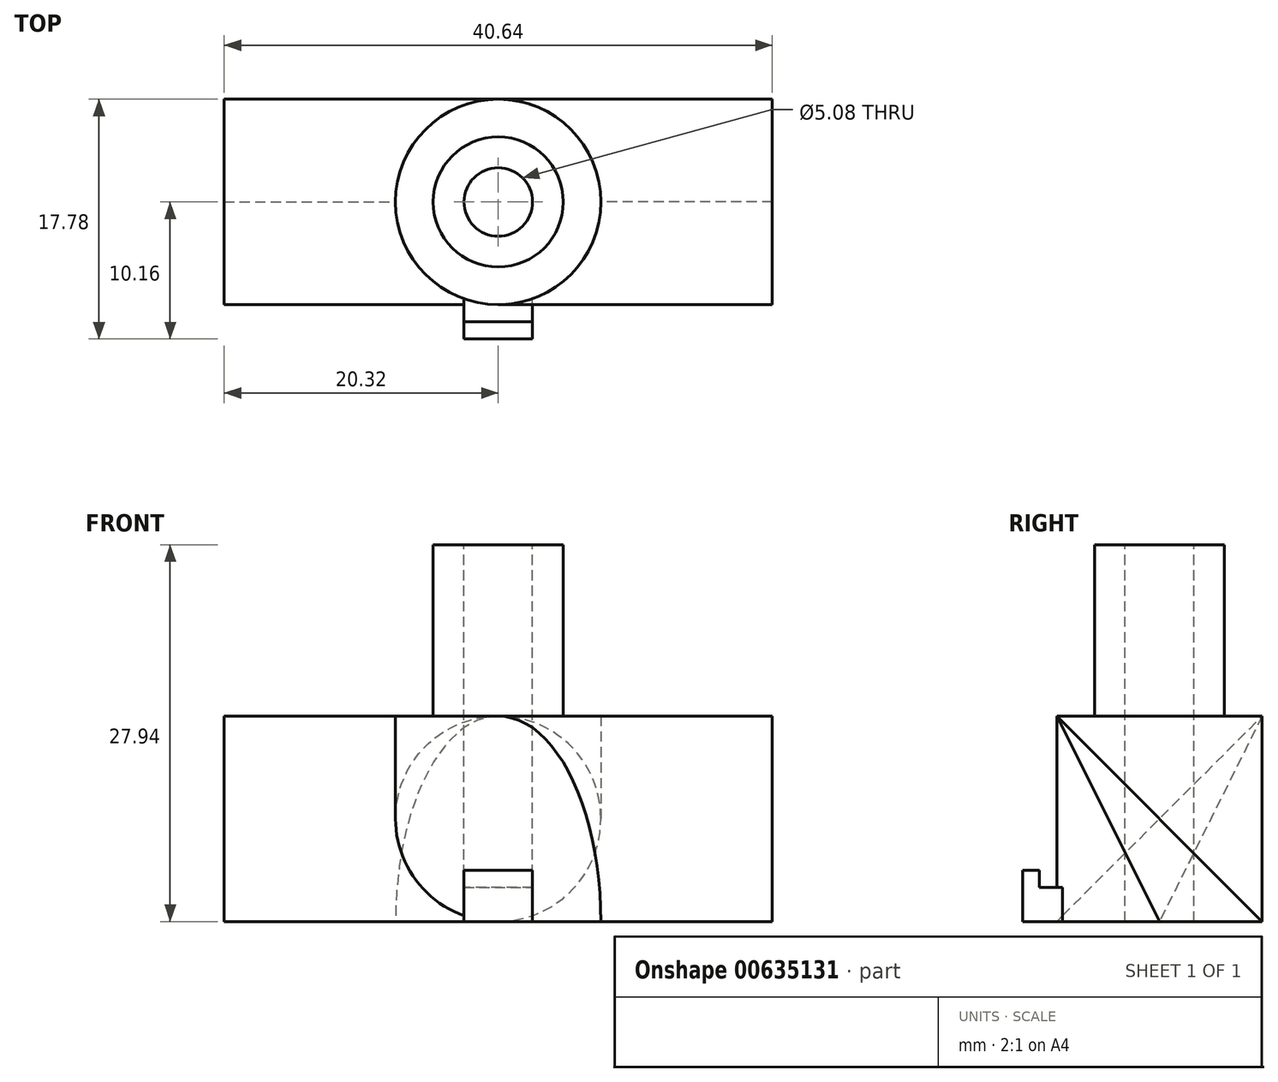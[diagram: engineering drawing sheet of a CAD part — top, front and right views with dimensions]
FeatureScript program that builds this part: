
annotation { "Feature Type Name" : "Feature", "Feature Type Description" : "" }
export const myFeature = defineFeature(function(context is Context, id is Id, definition is map)
    precondition{}
    {
        {
            var Q0;
            Q0=qCreatedBy(makeId("Top.planeOp"),FACE);
            var sketch = newSketch(context, id + "F0", { "sketchPlane" : qUnion([Q0])});
            skCircle(sketch, "E0", {"center": v(0, 0) * mm, "radius": 7.62 * mm});
            skSolve(sketch);
        }
        {
            var Q0;
            Q0=makeQuery(id+"F0.imprint","IMPRINT",FACE,{"disambiguationData":[TD([[makeQuery(id+"F0.imprint","IMPRINT",EDGE,{"derivedFrom":sQuery(id+"F0.wireOp",EDGE,"E0")}),1.0]])]});
            extrude(context, id + "F1", {"entities" : qUnion([Q0]), "depth" : 15.24 * mm, "offsetDistance" : 25.4 * mm});
        }
        {
            var Q0;
            Q0=qCreatedBy(makeId("Right.planeOp"),FACE);
            var sketch = newSketch(context, id + "F2", { "sketchPlane" : qUnion([Q0])});
            skLineSegment(sketch, "E1", {"start": v(0, 0) * mm, "end": v(7.62, 0) * mm});
            skLineSegment(sketch, "E2", {"start": v(7.62, 0) * mm, "end": v(-7.62, 15.24) * mm});
            skLineSegment(sketch, "E3", {"start": v(-7.62, 15.24) * mm, "end": v(0, 0) * mm});
            skSolve(sketch);
        }
        {
            var Q0;
            Q0=qSketchRegion(id+"F2",true);
            extrude(context, id + "F3", {"entities" : qUnion([Q0]), "depth" : 20.32 * mm, "offsetDistance" : 25.4 * mm});
        }
        {
            var Q0;
            Q0=qCreatedBy(makeId("Front.planeOp"),FACE);
            var sketch = newSketch(context, id + "F4", { "sketchPlane" : qUnion([Q0])});
            skLineSegment(sketch, "E4", {"start": v(0, 0) * mm, "end": v(0, 35.17) * mm, "construction": true});
            skSolve(sketch);
        }
        {
            var Q0;
            Q0=makeQuery(id+"F3.opExtrude","SWEPT_BODY",BODY,{"disambiguationData":[OSD([sQuery(id+"F2.wireOp",EDGE,"E1"),sQuery(id+"F2.wireOp",EDGE,"E2"),sQuery(id+"F2.wireOp",EDGE,"E3")])]});
            var Q1;
            Q1=sQuery(id+"F4.wireOp",EDGE,"E4");
            circularPattern(context, id + "F5", {"operationType" : NewBodyOperationType.ADD, "entities" : qUnion([Q0]), "axis" : qUnion([Q1]), "angle" : 360 * degree, "instanceCount" : 2, "equalSpace" : true});
        }
        {
            var Q0;
            Q0=qCreatedBy(makeId("Front.planeOp"),FACE);
            var sketch = newSketch(context, id + "F6", { "sketchPlane" : qUnion([Q0])});
            skLineSegment(sketch, "E5.bottom", {"start": v(-2.54, 2.54) * mm, "end": v(2.54, 2.54) * mm});
            skLineSegment(sketch, "E5.top", {"start": v(-2.54, 0) * mm, "end": v(2.54, 0) * mm});
            skLineSegment(sketch, "E5.left", {"start": v(-2.54, 2.54) * mm, "end": v(-2.54, 0) * mm});
            skLineSegment(sketch, "E5.right", {"start": v(2.54, 2.54) * mm, "end": v(2.54, 0) * mm});
            skSolve(sketch);
        }
        {
            var Q0;
            Q0=qSketchRegion(id+"F6",true);
            extrude(context, id + "F7", {"entities" : qUnion([Q0]), "operationType" : NewBodyOperationType.ADD, "depth" : 10.16 * mm, "offsetDistance" : 25.4 * mm});
        }
        {
            var Q0;
            Q0=makeQuery(id+"F7.opExtrude","SWEPT_FACE",FACE,{"disambiguationData":[OSD([sQuery(id+"F6.wireOp",EDGE,"E5.bottom")])]});
            var sketch = newSketch(context, id + "F8", { "sketchPlane" : qUnion([Q0])});
            skLineSegment(sketch, "E6.bottom", {"start": v(2.54, -10.16) * mm, "end": v(-2.54, -10.16) * mm});
            skLineSegment(sketch, "E6.top", {"start": v(2.54, -8.9) * mm, "end": v(-2.54, -8.9) * mm});
            skLineSegment(sketch, "E6.left", {"start": v(2.54, -10.16) * mm, "end": v(2.54, -8.9) * mm});
            skLineSegment(sketch, "E6.right", {"start": v(-2.54, -10.16) * mm, "end": v(-2.54, -8.9) * mm});
            skSolve(sketch);
        }
        {
            var Q0;
            Q0=makeQuery(id+"F8.imprint","IMPRINT",FACE,{"disambiguationData":[TD([[makeQuery(id+"F8.imprint","IMPRINT",EDGE,{"derivedFrom":sQuery(id+"F8.wireOp",EDGE,"E6.bottom")}),1.0]])]});
            extrude(context, id + "F9", {"entities" : qUnion([Q0]), "operationType" : NewBodyOperationType.ADD, "depth" : 1.27 * mm, "offsetDistance" : 25.4 * mm});
        }
        {
            var Q0;
            Q0=makeQuery(id+"F1.opExtrude","CAP_FACE",FACE,{"disambiguationData":[OSD([sQuery(id+"F0.wireOp",EDGE,"E0")])],"isStart":false});
            var sketch = newSketch(context, id + "F10", { "sketchPlane" : qUnion([Q0])});
            skCircle(sketch, "E7", {"center": v(0, 0) * mm, "radius": 2.54 * mm});
            skSolve(sketch);
        }
        {
            var Q0;
            Q0=qSketchRegion(id+"F10",true);
            extrude(context, id + "F11", {"entities" : qUnion([Q0]), "operationType" : NewBodyOperationType.REMOVE, "endBound" : BoundingType.THROUGH_ALL, "oppositeDirection" : true, "depth" : 13.97 * mm, "offsetDistance" : 25.4 * mm});
        }
        {
            var Q0;
            Q0=makeQuery(id+"F1.opExtrude","CAP_FACE",FACE,{"disambiguationData":[OSD([sQuery(id+"F0.wireOp",EDGE,"E0")])],"isStart":false});
            var sketch = newSketch(context, id + "F12", { "sketchPlane" : qUnion([Q0])});
            skCircle(sketch, "E8", {"center": v(0, 0) * mm, "radius": 4.83 * mm});
            skSolve(sketch);
        }
        {
            var Q0;
            Q0=makeQuery(id+"F12.imprint","IMPRINT",FACE,{"disambiguationData":[TD([[makeQuery(id+"F12.imprint","IMPRINT",EDGE,{"derivedFrom":sQuery(id+"F12.wireOp",EDGE,"E8")}),1.0]])]});
            extrude(context, id + "F13", {"entities" : qUnion([Q0]), "operationType" : NewBodyOperationType.ADD, "depth" : 12.7 * mm, "offsetDistance" : 25.4 * mm});
        }
    });
